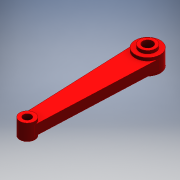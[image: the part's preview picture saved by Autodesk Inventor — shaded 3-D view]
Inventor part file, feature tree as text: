
AUTODESK INVENTOR PART (.ipt)
format: ipt  version: 2016 (Build 200138000, 138)  size: 135,168 bytes
history: native  units: mm
features: projected_geometry x5, extrude x4, sketch x4
ambient origin geometry x8: Origin, YZ Plane, XZ Plane, XY Plane, X Axis, Y Axis, Z Axis, Center Point
bodies: Solid1 (feature_tree)
feature tree (13):
  extrude  "Extrusion1"  Depth=15.0mm
  extrude  "Extrusion2"  Depth=10.0mm TaperAngle=0.0deg
  extrude  "Extrusion3"  Depth=16.0mm
  extrude  "Extrusion4"  Depth=10.0mm
  sketch  "Sketch1"  dims[d0=25.0mm d1=15.0mm]
  sketch  "Sketch2"  dims[d2=120.0mm d3=10.0mm d4=0.0mm]
  projected_geometry  "Projected Loop1"
  sketch  "Sketch3"  dims[d5=16.0mm d6=0.0mm d7=16.0mm]
  projected_geometry  "Projected Loop2"
  sketch  "Sketch4"  dims[d8=22.0mm d9=0.0mm d10=10.0mm d11=8.0mm d12=22.0mm d13=0.0mm]
  projected_geometry  "Projected Loop3"
  projected_geometry  "Projected Loop4"
  projected_geometry  "Projected Loop5"
